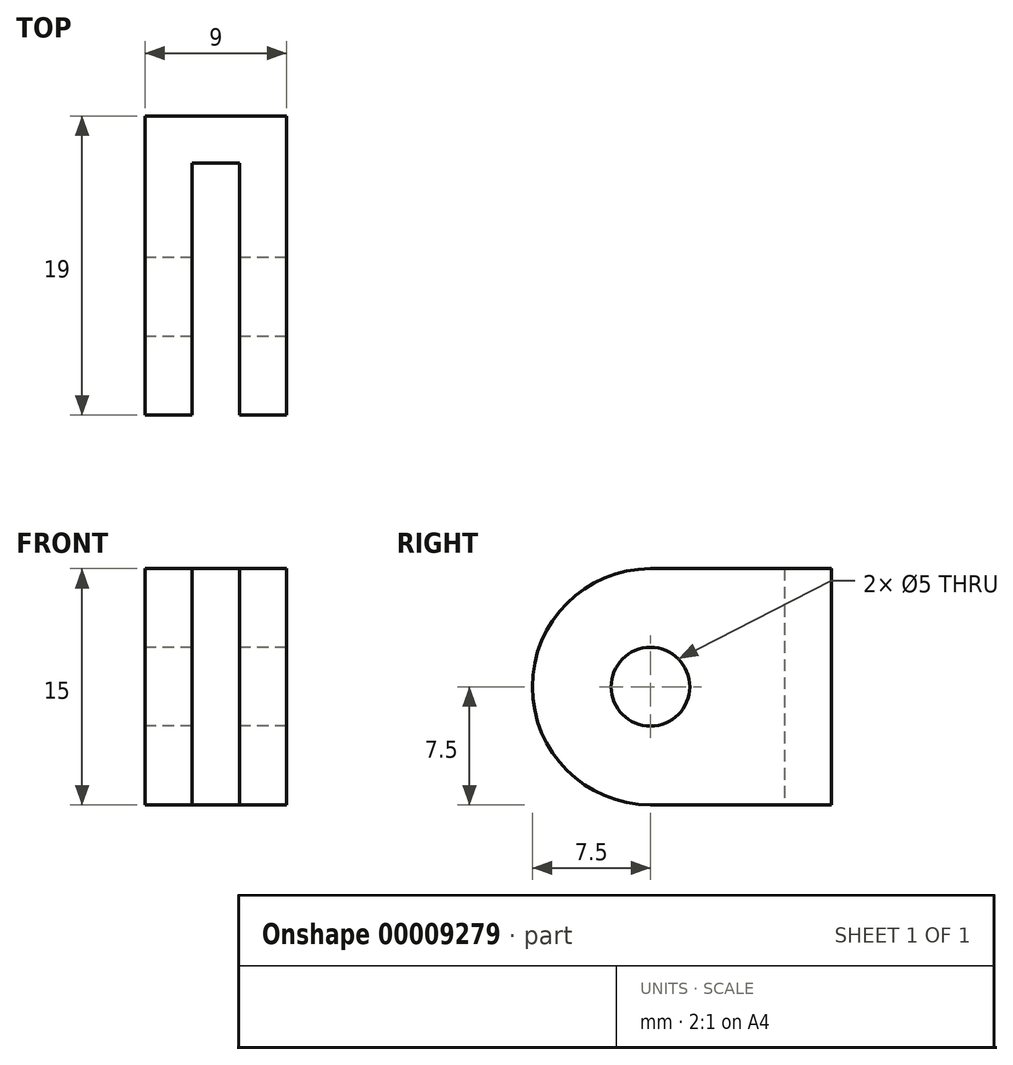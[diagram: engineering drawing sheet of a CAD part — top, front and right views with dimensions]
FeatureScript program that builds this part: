
annotation { "Feature Type Name" : "Feature", "Feature Type Description" : "" }
export const myFeature = defineFeature(function(context is Context, id is Id, definition is map)
    precondition{}
    {
        {
            var Q0;
            Q0=qCreatedBy(makeId("Top.planeOp"),FACE);
            var sketch = newSketch(context, id + "F0", { "sketchPlane" : qUnion([Q0])});
            skLineSegment(sketch, "E0", {"start": v(0, 0) * mm, "end": v(0, -34.87) * mm, "construction": true});
            skLineSegment(sketch, "E1", {"start": v(0, 0) * mm, "end": v(-4.5, 0) * mm});
            skLineSegment(sketch, "E2", {"start": v(-4.5, 0) * mm, "end": v(-4.5, -19) * mm});
            skLineSegment(sketch, "E3", {"start": v(-4.5, -19) * mm, "end": v(-1.5, -19) * mm});
            skLineSegment(sketch, "E4", {"start": v(-1.5, -19) * mm, "end": v(-1.5, -3) * mm});
            skLineSegment(sketch, "E5", {"start": v(-1.5, -3) * mm, "end": v(0, -3) * mm});
            skLineSegment(sketch, "E6.MirrorCS", {"start": v(1.5, -3) * mm, "end": v(0, -3) * mm});
            skLineSegment(sketch, "E7.MirrorCS", {"start": v(4.5, -19) * mm, "end": v(1.5, -19) * mm});
            skLineSegment(sketch, "E8.MirrorCS", {"start": v(0, 0) * mm, "end": v(4.5, 0) * mm});
            skLineSegment(sketch, "E9.MirrorCS", {"start": v(4.5, 0) * mm, "end": v(4.5, -19) * mm});
            skLineSegment(sketch, "E10.MirrorCS", {"start": v(1.5, -19) * mm, "end": v(1.5, -3) * mm});
            skSolve(sketch);
        }
        {
            var Q0;
            Q0 = qSketchRegion(id + "F0", true);
            extrude(context, id + "F1", {"entities" : qUnion([Q0]), "endBound" : BoundingType.SYMMETRIC, "depth" : 15 * mm});
        }
        {
            var Q0;
            Q0=makeQuery(id+"F1.opExtrude","SWEPT_FACE",FACE,{"disambiguationData":[OSD([sQuery(id+"F0.wireOp",EDGE,"E2")])]});
            var sketch = newSketch(context, id + "F2", { "sketchPlane" : qUnion([Q0])});
            skArc(sketch, "E11", {"start": v(11.5, -7.5) * mm, "mid": v(19, 0) * mm, "end": v(11.5, 7.5) * mm});
            skPoint(sketch, "E11.first.point", {"position": v(11.5, -7.5) * mm});
            skPoint(sketch, "E11.second.point", {"position": v(19, 0) * mm});
            skPoint(sketch, "E11.third.point", {"position": v(11.5, 7.5) * mm});
            skLineSegment(sketch, "E12", {"start": v(11.5, -7.5) * mm, "end": v(11.5, 7.5) * mm, "construction": true});
            skLineSegment(sketch, "E13.0", {"start": v(11.5, -7.5) * mm, "end": v(19, -7.5) * mm});
            skLineSegment(sketch, "E14.0", {"start": v(19, 7.5) * mm, "end": v(19, -7.5) * mm});
            skLineSegment(sketch, "E15.0", {"start": v(11.5, 7.5) * mm, "end": v(19, 7.5) * mm});
            skPoint(sketch, "E16.orphan", {"position": v(0, -7.5) * mm});
            skPoint(sketch, "E17.orphan", {"position": v(0, 7.5) * mm});
            skSolve(sketch);
        }
        {
            var Q0;
            Q0 = qSketchRegion(id + "F2", true);
            var Q1;
            Q1=makeQuery(id+"F1.opExtrude","SWEPT_FACE",FACE,{"disambiguationData":[OSD([sQuery(id+"F0.wireOp",EDGE,"E9.MirrorCS")])]});
            extrude(context, id + "F3", {"entities" : qUnion([Q0]), "operationType" : NewBodyOperationType.REMOVE, "endBound" : BoundingType.UP_TO_SURFACE, "oppositeDirection" : true, "endBoundEntityFace" : qUnion([Q1]), "depth" : 25 * mm});
        }
        {
            var Q0;
            Q0=sQuery(id+"F2.wireOp",VERTEX,"E11.center");
            var Q1;
            Q1=makeQuery(id+"F1.opExtrude","SWEPT_BODY",BODY,{"disambiguationData":[OSD([sQuery(id+"F0.wireOp",EDGE,"E1"),sQuery(id+"F0.wireOp",EDGE,"E2"),sQuery(id+"F0.wireOp",EDGE,"E3"),sQuery(id+"F0.wireOp",EDGE,"E4"),sQuery(id+"F0.wireOp",EDGE,"E5"),sQuery(id+"F0.wireOp",EDGE,"E6.MirrorCS"),sQuery(id+"F0.wireOp",EDGE,"E7.MirrorCS"),sQuery(id+"F0.wireOp",EDGE,"E8.MirrorCS"),sQuery(id+"F0.wireOp",EDGE,"E9.MirrorCS"),sQuery(id+"F0.wireOp",EDGE,"E10.MirrorCS")])]});
            hole(context, id + "F4", {"style" : HoleStyle.SIMPLE, "holeDiameter" : 5 * mm, "endStyle" : HoleEndStyle.THROUGH, "locations" : qUnion([Q0]), "scope" : qUnion([Q1])});
        }
    });
